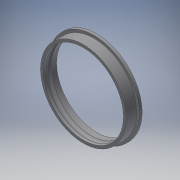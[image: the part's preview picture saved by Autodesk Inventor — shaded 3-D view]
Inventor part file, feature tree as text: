
AUTODESK INVENTOR PART (.ipt)
format: ipt  version: 2017 (Build 210142000, 142)  size: 143,360 bytes
history: native  units: in
note: dims shown in document units (in); Inventor stores cm internally (conversion verified against a paired STEP export)
features: sketch x2, revolve x1, extrude x1, projected_geometry x1
ambient origin geometry x8: Origin, YZ Plane, XZ Plane, XY Plane, X Axis, Y Axis, Z Axis, Center Point
bodies: Solid1 (feature_tree)
feature tree (5):
  revolve  "Revolution1"  [1 undecoded]
  extrude  "Extrusion1"  Depth=0.25in
  sketch  "Sketch1"  dims[d1=1.875in d2=0.124in]
  sketch  "Sketch2"  dims[d3=0.25in d4=0.25in d5=0.0675in d6=0.135in d7=90.0deg d8=0.125in d9=0.125in d10=0.0in]
  projected_geometry  "Projected Loop1"
note: 1 required parameter value undecoded (feature->parameter linkage not recoverable at this tier; creation-order binding heuristic only, values carry confidence <= 0.55)
